# Revit family: 2056234 Sylvania Lighting Fixture MYD ADJ SQ BLK 3K PHDIM SILBEZ
name_source: partatom
category: Lighting Fixtures
revit_build: Autodesk Revit 2016 (Build: 20150220_1215(x64)
units: mm (PartAtom-declared; Revit-internal decimal feet)

## family parameters
Cut with Voids When Loaded = Yes
Host = Face
Light Source = No
OmniClass Number = 23.80.70.00
OmniClass Title = Lighting
Part Type = Normal
Room Calculation Point = No
Round Connector Dimension = Use Diameter
Shared = No

## types (1)
- 2056234 MYD ADJ SQ BLK 3K PHDIM SILBEZ
    Apparent Load = 10 VA
    Assembly Code = D5020200
    AssetType = Fixed
    ClassificationName = Uniclass2015
    ClassificationValue = EF_70_80
    Cost = 0 $
    Default Elevation = 1219 mm
    Description = MYD ADJ SQ BLK 3K PHDIM SILBEZ
    DocumentationLiterature = http://www.sylvania-lighting.com
    DraftAngle_SYL = 2.50°
    DraftIn_SYL = 1 mm  [stored 0.00328084 ft]
    DraftOut_SYL = 2 mm  [stored 0.00656168 ft]
    DurationUnit = hours
    ElectricShockClassification = Class II
    ExpectedLife = 50000
    HeightBezel_SYL = 4 mm  [stored 0.0131234 ft]
    HeightTop_SYL = 40 mm  [stored 0.131234 ft]
    HeightVoid_SYL = 16 mm  [stored 0.0524934 ft]
    IfcExportAs = IfcLightFixtureType
    IfcExportType = IfcLightFixtureType
    ImpactProtectionIndex = IK02
    IngressProtection = IP20
    Keynote = 16500
    Lamp = LED
    LampColourRenderingIndex = 85
    LampColourTemperature = 3000 K
    LampNominalLuminous = 702 lm
    LampsType = LED
    LightOutputRatio = 100
    LuminousEfficacy = 70 lm/W
    Manufacturer = Feilo Sylvania
    ManufacturerName = Feilo Sylvania
    Material = polycarbonate housing
    Material_1_SYL = Body-Sylvania-MyriadAdjustableRound-Black
    Material_2_SYL = <By Category>
    Material_3_SYL = <By Category>
    Material_4_SYL = Body-Sylvania-MyriadAdjustableRound-Silver
    Model = MYD ADJ SQ BLK 3K PHDIM SILBEZ
    ModelNumber = 2056234
    ModelReference = MYD ADJ SQ BLK 3K PHDIM SILBEZ
    Name = MYD ADJ SQ BLK 3K PHDIM SILBEZ
    NominalDepth = 76 mm  [stored 0.249344 ft]
    NominalHeight = 115 mm  [stored 0.377297 ft]
    NominalLength = 0 mm  [stored 0 ft]
    PowerConsumption = 10 W
    PowerFactor = 0
    SphereRadius_FEILO = 31 mm  [stored 0.101706 ft]
    Type Image = <None>
    TypeLamp_SYL = Myriad Adjustable Square Lamp : 2056234 MYD ADJ SQ BLK 3K PHDIM SILBEZ
    TypeName = MYD ADJ SQ BLK 3K PHDIM SILBEZ
    URL = http://www.sylvania-lighting.com
    Voltage = 0 V
    Weight = 0.38 kg
    WidthBezel_SYL = 7 mm  [stored 0.0229659 ft]
    WidthCutOut_SYL = 72 mm  [stored 0.23622 ft]
    Width_SYL = 86 mm  [stored 0.282152 ft]

note: [stored X ft] marks values corroborated as IEEE doubles in the binary element streams (Revit-internal decimal feet)

## geometry (parser evidence)
native form markers: Sweep x10
no freeform markers — native parametric forms only
